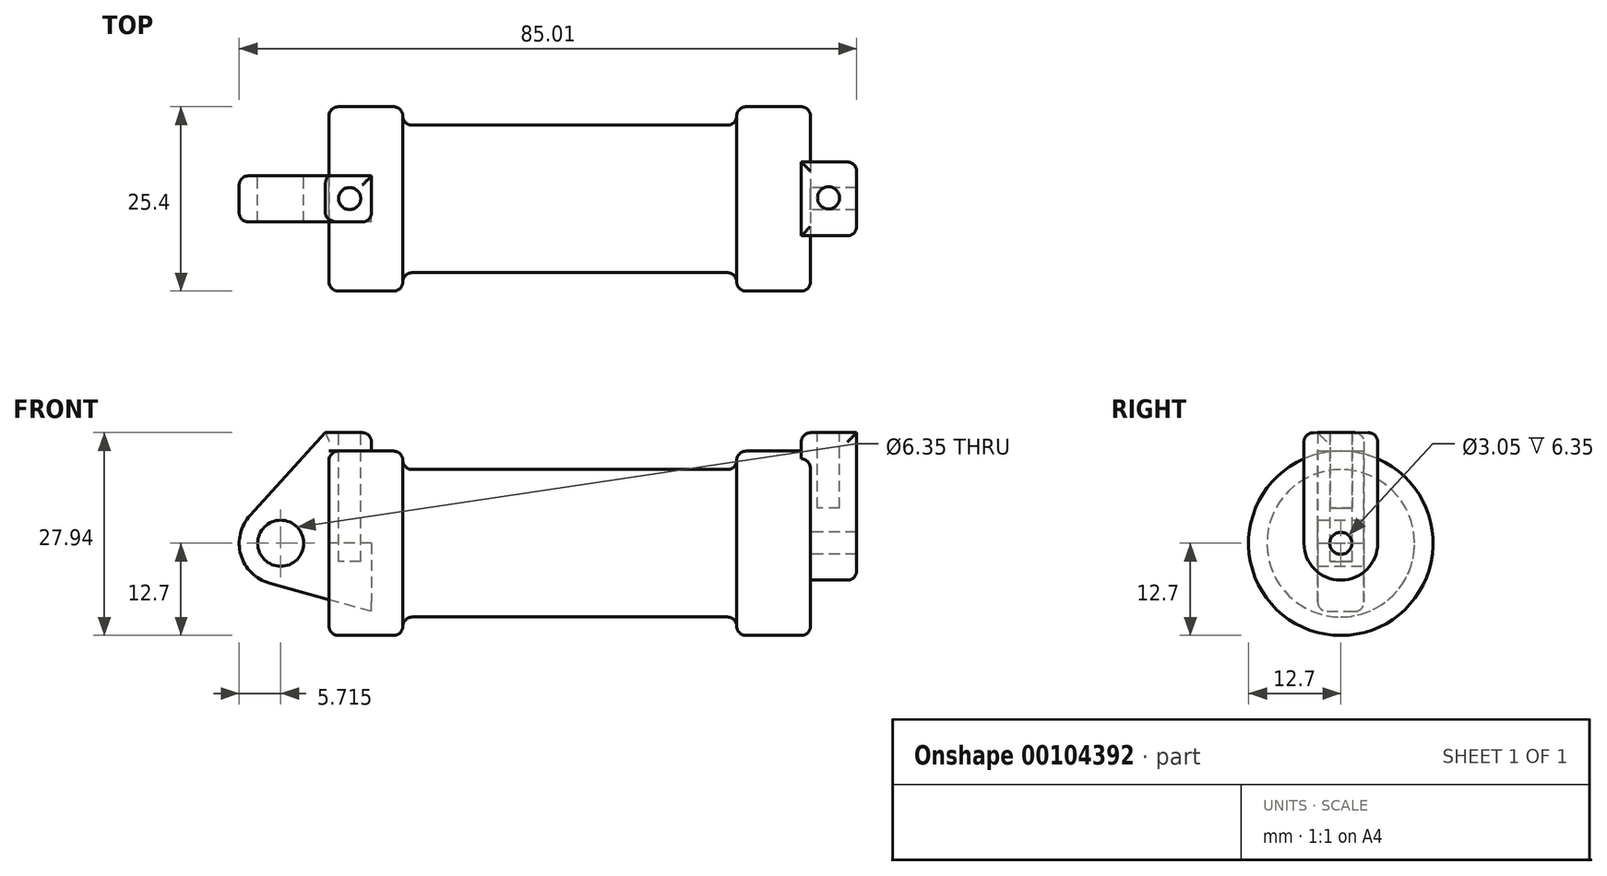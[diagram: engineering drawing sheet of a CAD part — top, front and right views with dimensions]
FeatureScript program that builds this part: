
annotation { "Feature Type Name" : "Feature", "Feature Type Description" : "" }
export const myFeature = defineFeature(function(context is Context, id is Id, definition is map)
    precondition{}
    {
        {
            var Q0;
            Q0=qCreatedBy(makeId("Front.planeOp"),FACE);
            var sketch = newSketch(context, id + "F0", { "sketchPlane" : qUnion([Q0])});
            skLineSegment(sketch, "E0", {"start": v(0, 0) * mm, "end": v(0, 12.7) * mm});
            skLineSegment(sketch, "E1", {"start": v(0, 12.7) * mm, "end": v(10.16, 12.7) * mm});
            skLineSegment(sketch, "E2", {"start": v(10.16, 12.7) * mm, "end": v(10.16, 10.16) * mm});
            skLineSegment(sketch, "E3", {"start": v(10.16, 10.16) * mm, "end": v(56.13, 10.16) * mm});
            skLineSegment(sketch, "E4", {"start": v(56.13, 10.16) * mm, "end": v(56.13, 12.7) * mm});
            skLineSegment(sketch, "E5", {"start": v(56.13, 12.7) * mm, "end": v(66.3, 12.7) * mm});
            skLineSegment(sketch, "E6", {"start": v(66.3, 12.7) * mm, "end": v(66.3, 0) * mm});
            skLineSegment(sketch, "E7", {"start": v(66.3, 0) * mm, "end": v(0, 0) * mm});
            skLineSegment(sketch, "E8", {"start": v(5.84, 15.24) * mm, "end": v(-0.5, 15.24) * mm});
            skLineSegment(sketch, "E9", {"start": v(-0.5, 15.24) * mm, "end": v(-10.88, 3.85) * mm});
            skLineSegment(sketch, "E10", {"start": v(0, 0) * mm, "end": v(-6.65, 0) * mm});
            skCircle(sketch, "E11", {"center": v(-6.65, 0) * mm, "radius": 5.72 * mm});
            skCircle(sketch, "E12", {"center": v(-6.65, 0) * mm, "radius": 3.18 * mm});
            skLineSegment(sketch, "E13", {"start": v(5.84, 15.24) * mm, "end": v(5.84, -9.4) * mm});
            skLineSegment(sketch, "E14", {"start": v(5.84, -9.4) * mm, "end": v(-8.18, -5.5) * mm});
            skSolve(sketch);
        }
        {
            var Q0;
            {var subQ0=sQuery(id+"F0.wireOp",EDGE,"E2");Q0=makeQuery(id+"F0.imprint","IMPRINT",FACE,{"disambiguationData":[TD([[makeQuery(id+"F0.imprint","IMPRINT",EDGE,{"derivedFrom":subQ0}),-1.0]])]});}
            var Q1;
            {var subQ0=sQuery(id+"F0.wireOp",EDGE,"E0");Q1=makeQuery(id+"F0.imprint","IMPRINT",FACE,{"disambiguationData":[TD([[makeQuery(id+"F0.imprint","IMPRINT",EDGE,{"derivedFrom":subQ0}),-1.0]])]});}
            var Q2;
            Q2=sQuery(id+"F0.wireOp",EDGE,"E7");
            revolve(context, id + "F1", {"entities" : qUnion([Q0, Q1]), "axis" : qUnion([Q2]), "revolveType" : RevolveType.FULL});
        }
        {
            var Q0;
            {var subQ4=sQuery(id+"F0.wireOp",EDGE,"E12");Q0=makeQuery(id+"F0.imprint","IMPRINT",FACE,{"disambiguationData":[TD([[makeQuery(id+"F0.imprint","IMPRINT",EDGE,{"derivedFrom":subQ4}),-1.0]])]});}
            var Q1;
            {var subQ0=sQuery(id+"F0.wireOp",EDGE,"E14");Q1=makeQuery(id+"F0.imprint","IMPRINT",FACE,{"disambiguationData":[TD([[makeQuery(id+"F0.imprint","IMPRINT",EDGE,{"derivedFrom":subQ0}),-1.0]])]});}
            var Q2;
            {var subQ3=sQuery(id+"F0.wireOp",EDGE,"E0");Q2=makeQuery(id+"F0.imprint","IMPRINT",FACE,{"disambiguationData":[TD([[makeQuery(id+"F0.imprint","IMPRINT",EDGE,{"derivedFrom":subQ3}),1.0]])]});}
            extrude(context, id + "F2", {"entities" : qUnion([Q0, Q1, Q2]), "endBound" : BoundingType.SYMMETRIC, "depth" : 6.35 * mm});
        }
        {
            var Q0;
            Q0=makeQuery(id+"F1.opRevolve","SWEPT_FACE",FACE,{"disambiguationData":[OSD([sQuery(id+"F0.wireOp",EDGE,"E6")])]});
            var sketch = newSketch(context, id + "F3", { "sketchPlane" : qUnion([Q0])});
            skCircle(sketch, "E15", {"center": v(0, 0) * mm, "radius": 1.52 * mm});
            skCircle(sketch, "E16", {"center": v(0, 0) * mm, "radius": 5.08 * mm});
            skLineSegment(sketch, "E17", {"start": v(-5.08, 0) * mm, "end": v(-5.08, 15.23) * mm});
            skLineSegment(sketch, "E18", {"start": v(5.08, 0) * mm, "end": v(5.08, 15.24) * mm});
            skLineSegment(sketch, "E19", {"start": v(5.08, 15.24) * mm, "end": v(-5.08, 15.23) * mm});
            skSolve(sketch);
        }
        {
            var Q0;
            {var subQ0=sQuery(id+"F3.wireOp",EDGE,"E19");Q0=makeQuery(id+"F3.imprint","IMPRINT",FACE,{"disambiguationData":[TD([[makeQuery(id+"F3.imprint","IMPRINT",EDGE,{"derivedFrom":subQ0}),1.0]])]});}
            var Q1;
            {var subQ0=sQuery(id+"F3.wireOp",EDGE,"E17");var subQ1=sQuery(id+"F3.wireOp",EDGE,"E16");var subQ2=makeQuery(id+"F3.imprint","INTERSECT",VERTEX,{"derivedFrom":[subQ1,subQ0]});Q1=makeQuery(id+"F3.imprint","IMPRINT",FACE,{"disambiguationData":[TD([[makeQuery(id+"F3.imprint","IMPRINT",EDGE,{"disambiguationData":[TD([[subQ2,1.0]])],"derivedFrom":subQ1}),-1.0]])]});}
            var Q2;
            Q2=makeQuery(id+"F3.imprint","IMPRINT",FACE,{"disambiguationData":[TD([[makeQuery(id+"F3.imprint","IMPRINT",EDGE,{"derivedFrom":sQuery(id+"F3.wireOp",EDGE,"E15")}),-1.0]])]});
            extrude(context, id + "F4", {"entities" : qUnion([Q0, Q1, Q2]), "operationType" : NewBodyOperationType.ADD, "depth" : 6.35 * mm});
        }
        {
            var Q0;
            Q0=makeQuery(id+"F4.opExtrude","CAP_FACE",FACE,{"disambiguationData":[OSD([sQuery(id+"F3.wireOp",EDGE,"E15"),sQuery(id+"F3.wireOp",EDGE,"E16"),sQuery(id+"F3.wireOp",EDGE,"E17"),sQuery(id+"F3.wireOp",EDGE,"E18"),sQuery(id+"F3.wireOp",EDGE,"E19")])],"isStart":true});
            extrude(context, id + "F5", {"entities" : qUnion([Q0]), "operationType" : NewBodyOperationType.ADD, "depth" : 1.27 * mm});
        }
        {
            var Q0;
            Q0=makeQuery(id+"F2.opExtrude","SWEPT_FACE",FACE,{"disambiguationData":[OSD([sQuery(id+"F0.wireOp",EDGE,"E8")])]});
            var sketch = newSketch(context, id + "F6", { "sketchPlane" : qUnion([Q0])});
            skCircle(sketch, "E20", {"center": v(68.79, 0.15) * mm, "radius": 1.52 * mm});
            skCircle(sketch, "E21", {"center": v(2.83, 0.05) * mm, "radius": 1.52 * mm});
            skSolve(sketch);
        }
        {
            var Q0;
            Q0=makeQuery(id+"F6.imprint","IMPRINT",FACE,{"disambiguationData":[TD([[makeQuery(id+"F6.imprint","IMPRINT",EDGE,{"derivedFrom":sQuery(id+"F6.wireOp",EDGE,"E21")}),1.0]])]});
            extrude(context, id + "F7", {"entities" : qUnion([Q0]), "oppositeDirection" : true, "depth" : 17.78 * mm});
        }
        {
            var Q0;
            Q0=makeQuery(id+"F6.imprint","IMPRINT",FACE,{"disambiguationData":[TD([[makeQuery(id+"F6.imprint","IMPRINT",EDGE,{"derivedFrom":sQuery(id+"F6.wireOp",EDGE,"E20")}),1.0]])]});
            extrude(context, id + "F8", {"entities" : qUnion([Q0]), "oppositeDirection" : true, "depth" : 10.4 * mm});
        }
        {
            var Q0;
            Q0=makeQuery(id+"F1.opRevolve","SWEPT_FACE",FACE,{"disambiguationData":[OSD([sQuery(id+"F0.wireOp",EDGE,"E1")])]});
            var Q1;
            Q1=makeQuery(id+"F1.opRevolve","SWEPT_EDGE",EDGE,{"disambiguationData":[OSD([sQuery(id+"F0.wireOp",EDGE,"E2"),sQuery(id+"F0.wireOp",EDGE,"E3")])]});
            fillet(context, id + "F9", {"entities" : qUnion([Q0, Q1]), "radius" : 1.27 * mm, "tangentPropagation" : true, "allowEdgeOverflow" : false});
        }
        {
            var Q0;
            Q0=makeQuery(id+"F1.opRevolve","SWEPT_EDGE",EDGE,{"disambiguationData":[OSD([sQuery(id+"F0.wireOp",EDGE,"E4"),sQuery(id+"F0.wireOp",EDGE,"E5")])]});
            var Q1;
            Q1=makeQuery(id+"F1.opRevolve","SWEPT_EDGE",EDGE,{"disambiguationData":[OSD([sQuery(id+"F0.wireOp",EDGE,"E3"),sQuery(id+"F0.wireOp",EDGE,"E4")])]});
            var Q2;
            Q2=makeQuery(id+"F4.boolean.opBoolean","SPLIT",EDGE,{"disambiguationData":[OD(1.0)],"derivedFrom":makeQuery(id+"F1.opRevolve","SWEPT_EDGE",EDGE,{"disambiguationData":[OSD([sQuery(id+"F0.wireOp",EDGE,"E5"),sQuery(id+"F0.wireOp",EDGE,"E6")])]})});
            fillet(context, id + "F10", {"entities" : qUnion([Q0, Q1, Q2]), "radius" : 1.27 * mm, "tangentPropagation" : true, "allowEdgeOverflow" : false});
        }
        {
            var Q0;
            Q0=makeQuery(id+"F2.opExtrude","CAP_EDGE",EDGE,{"disambiguationData":[OSD([sQuery(id+"F0.wireOp",EDGE,"E11")])],"isStart":false});
            var Q1;
            Q1=makeQuery(id+"F2.opExtrude","CAP_EDGE",EDGE,{"disambiguationData":[OSD([sQuery(id+"F0.wireOp",EDGE,"E9")])],"isStart":true});
            var Q2;
            {var subQ0=sQuery(id+"F0.wireOp",EDGE,"E13");Q2=makeQuery(id+"F2.opExtrude","CAP_EDGE",EDGE,{"disambiguationData":[OSD([subQ0]),TDD([makeQuery(id+"F0.imprint","IMPRINT",EDGE,{"disambiguationData":[TD([[makeQuery(id+"F0.imprint","INTERSECT",VERTEX,{"derivedFrom":[sQuery(id+"F0.wireOp",EDGE,"E8"),subQ0]}),-1.0]])],"derivedFrom":subQ0})])],"isStart":false});}
            var Q3;
            Q3=makeQuery(id+"F2.opExtrude","CAP_EDGE",EDGE,{"disambiguationData":[OSD([sQuery(id+"F0.wireOp",EDGE,"E8")])],"isStart":true});
            var Q4;
            Q4=makeQuery(id+"F2.opExtrude","SWEPT_EDGE",EDGE,{"disambiguationData":[OSD([sQuery(id+"F0.wireOp",EDGE,"E8"),sQuery(id+"F0.wireOp",EDGE,"E13")])]});
            fillet(context, id + "F11", {"entities" : qUnion([Q0, Q1, Q2, Q3, Q4]), "radius" : 1.27 * mm, "tangentPropagation" : true, "allowEdgeOverflow" : false});
        }
        {
            var Q0;
            Q0=makeQuery(id+"F4.opExtrude","CAP_EDGE",EDGE,{"disambiguationData":[OSD([sQuery(id+"F3.wireOp",EDGE,"E16")])],"isStart":false});
            var Q1;
            Q1=makeQuery(id+"F4.opExtrude","CAP_EDGE",EDGE,{"disambiguationData":[OSD([sQuery(id+"F3.wireOp",EDGE,"E17")])],"isStart":false});
            var Q2;
            {var subQ0=sQuery(id+"F3.wireOp",EDGE,"E19");var subQ1=sQuery(id+"F3.wireOp",EDGE,"E17");Q2=makeQuery(id+"F5.boolean.opBoolean","MERGE",EDGE,{"derivedFrom":[makeQuery(id+"F4.opExtrude","SWEPT_EDGE",EDGE,{"disambiguationData":[OSD([subQ1,subQ0])]}),makeQuery(id+"F5.opExtrude","SWEPT_EDGE",EDGE,{"disambiguationData":[OSD([subQ1,subQ0])]})]});}
            var Q3;
            {var subQ0=sQuery(id+"F3.wireOp",EDGE,"E19");var subQ1=sQuery(id+"F3.wireOp",EDGE,"E18");Q3=makeQuery(id+"F5.boolean.opBoolean","MERGE",EDGE,{"derivedFrom":[makeQuery(id+"F4.opExtrude","SWEPT_EDGE",EDGE,{"disambiguationData":[OSD([subQ1,subQ0])]}),makeQuery(id+"F5.opExtrude","SWEPT_EDGE",EDGE,{"disambiguationData":[OSD([subQ1,subQ0])]})]});}
            var Q4;
            Q4=makeQuery(id+"F5.opExtrude","CAP_EDGE",EDGE,{"disambiguationData":[OSD([sQuery(id+"F3.wireOp",EDGE,"E19")])],"isStart":false});
            fillet(context, id + "F12", {"entities" : qUnion([Q0, Q1, Q2, Q3, Q4]), "radius" : 1.27 * mm, "tangentPropagation" : true, "allowEdgeOverflow" : false});
        }
    });
